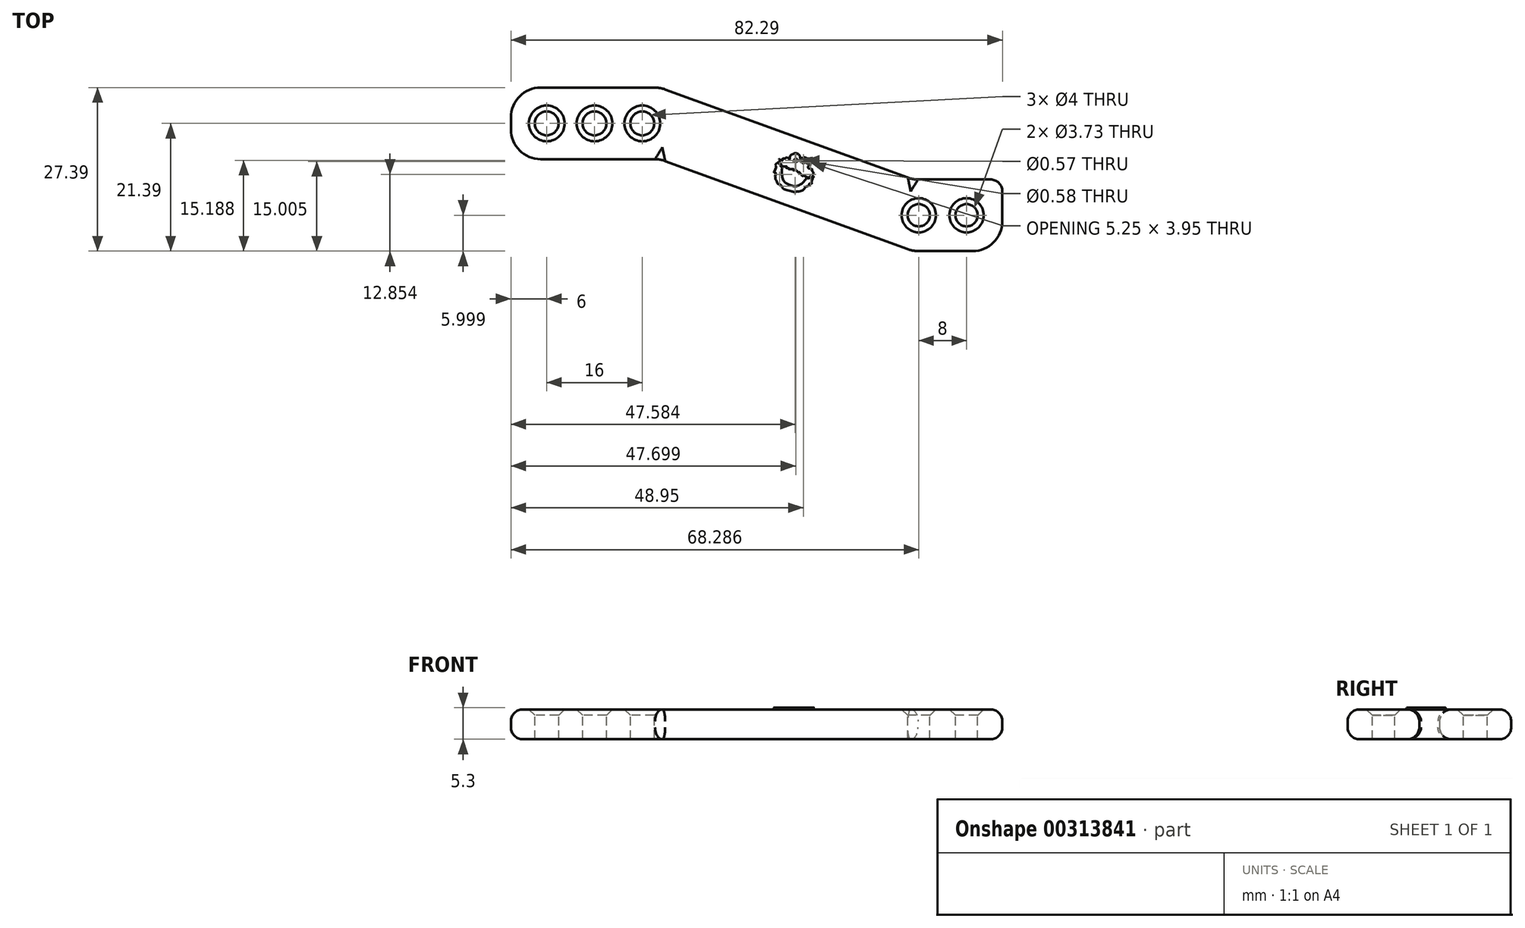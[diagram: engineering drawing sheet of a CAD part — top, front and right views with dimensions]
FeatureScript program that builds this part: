
annotation { "Feature Type Name" : "Feature", "Feature Type Description" : "" }
export const myFeature = defineFeature(function(context is Context, id is Id, definition is map)
    precondition{}
    {
        {
            var Q0;
            Q0=qCreatedBy(makeId("Top.planeOp"),FACE);
            var sketch = newSketch(context, id + "F0", { "sketchPlane" : qUnion([Q0])});
            skLineSegment(sketch, "E0.bottom", {"start": v(0, 0) * mm, "end": v(25, 0) * mm});
            skLineSegment(sketch, "E0.top", {"start": v(0, 12) * mm, "end": v(25, 12) * mm});
            skLineSegment(sketch, "E0.left", {"start": v(0, 0) * mm, "end": v(0, 12) * mm});
            skLineSegment(sketch, "E0.right", {"start": v(25, 0) * mm, "end": v(25, 12) * mm});
            skLineSegment(sketch, "E1.bottom", {"start": v(67.29, -3.4) * mm, "end": v(82.29, -3.4) * mm});
            skLineSegment(sketch, "E1.top", {"start": v(67.29, -15.4) * mm, "end": v(82.29, -15.4) * mm});
            skLineSegment(sketch, "E1.left", {"start": v(67.29, -3.4) * mm, "end": v(67.29, -15.4) * mm});
            skLineSegment(sketch, "E1.right", {"start": v(82.29, -3.4) * mm, "end": v(82.29, -15.4) * mm});
            skLineSegment(sketch, "E2", {"start": v(25, 12) * mm, "end": v(67.29, -3.4) * mm});
            skLineSegment(sketch, "E3", {"start": v(25, 0) * mm, "end": v(67.29, -15.4) * mm});
            skSolve(sketch);
        }
        {
            var Q0;
            Q0=makeQuery(id+"F0.imprint","IMPRINT",FACE,{"disambiguationData":[TD([[makeQuery(id+"F0.imprint","IMPRINT",EDGE,{"derivedFrom":sQuery(id+"F0.wireOp",EDGE,"E0.right")}),-1.0]])]});
            var Q1;
            Q1=makeQuery(id+"F0.imprint","IMPRINT",FACE,{"disambiguationData":[TD([[makeQuery(id+"F0.imprint","IMPRINT",EDGE,{"derivedFrom":sQuery(id+"F0.wireOp",EDGE,"E0.bottom")}),1.0]])]});
            var Q2;
            Q2=makeQuery(id+"F0.imprint","IMPRINT",FACE,{"disambiguationData":[TD([[makeQuery(id+"F0.imprint","IMPRINT",EDGE,{"derivedFrom":sQuery(id+"F0.wireOp",EDGE,"E1.bottom")}),-1.0]])]});
            extrude(context, id + "F1", {"entities" : qUnion([Q0, Q1, Q2]), "depth" : 5 * mm});
        }
        {
            var Q0;
            Q0=makeQuery(id+"F1.opExtrude","CAP_FACE",FACE,{"disambiguationData":[OSD([sQuery(id+"F0.wireOp",EDGE,"E0.bottom"),sQuery(id+"F0.wireOp",EDGE,"E0.top"),sQuery(id+"F0.wireOp",EDGE,"E0.left"),sQuery(id+"F0.wireOp",EDGE,"E1.bottom"),sQuery(id+"F0.wireOp",EDGE,"E1.top"),sQuery(id+"F0.wireOp",EDGE,"E1.right"),sQuery(id+"F0.wireOp",EDGE,"E2"),sQuery(id+"F0.wireOp",EDGE,"E3")])],"isStart":false});
            var sketch = newSketch(context, id + "F2", { "sketchPlane" : qUnion([Q0])});
            skCircle(sketch, "E4", {"center": v(6, 6) * mm, "radius": 2 * mm});
            skCircle(sketch, "E5", {"center": v(76.29, -9.4) * mm, "radius": 1.86 * mm});
            skCircle(sketch, "E6.1.0.0", {"center": v(14, 6) * mm, "radius": 2 * mm});
            skCircle(sketch, "E6.2.0.0", {"center": v(22, 6) * mm, "radius": 2 * mm});
            skLineSegment(sketch, "E6.direction1", {"start": v(6, 6) * mm, "end": v(14, 6) * mm, "construction": true});
            skCircle(sketch, "E7.1.0.0", {"center": v(68.29, -9.4) * mm, "radius": 1.86 * mm});
            skLineSegment(sketch, "E7.direction1", {"start": v(68.29, -9.4) * mm, "end": v(76.29, -9.4) * mm, "construction": true});
            skSolve(sketch);
        }
        {
            var Q0;
            Q0=makeQuery(id+"F2.imprint","IMPRINT",FACE,{"disambiguationData":[TD([[makeQuery(id+"F2.imprint","IMPRINT",EDGE,{"derivedFrom":sQuery(id+"F2.wireOp",EDGE,"E4")}),1.0]])]});
            var Q1;
            Q1=makeQuery(id+"F2.imprint","IMPRINT",FACE,{"disambiguationData":[TD([[makeQuery(id+"F2.imprint","IMPRINT",EDGE,{"derivedFrom":sQuery(id+"F2.wireOp",EDGE,"E6.1.0.0")}),1.0]])]});
            var Q2;
            Q2=makeQuery(id+"F2.imprint","IMPRINT",FACE,{"disambiguationData":[TD([[makeQuery(id+"F2.imprint","IMPRINT",EDGE,{"derivedFrom":sQuery(id+"F2.wireOp",EDGE,"E6.2.0.0")}),1.0]])]});
            var Q3;
            Q3=makeQuery(id+"F2.imprint","IMPRINT",FACE,{"disambiguationData":[TD([[makeQuery(id+"F2.imprint","IMPRINT",EDGE,{"derivedFrom":sQuery(id+"F2.wireOp",EDGE,"E7.1.0.0")}),1.0]])]});
            var Q4;
            Q4=makeQuery(id+"F2.imprint","IMPRINT",FACE,{"disambiguationData":[TD([[makeQuery(id+"F2.imprint","IMPRINT",EDGE,{"derivedFrom":sQuery(id+"F2.wireOp",EDGE,"E5")}),1.0]])]});
            extrude(context, id + "F3", {"entities" : qUnion([Q0, Q1, Q2, Q3, Q4]), "operationType" : NewBodyOperationType.REMOVE, "endBound" : BoundingType.UP_TO_NEXT, "oppositeDirection" : true, "depth" : 3 * mm});
        }
        {
            var Q0;
            Q0=makeQuery(id+"F1.opExtrude","CAP_EDGE",EDGE,{"disambiguationData":[OSD([sQuery(id+"F0.wireOp",EDGE,"E0.bottom")])],"isStart":false});
            var Q1;
            Q1=makeQuery(id+"F1.opExtrude","CAP_EDGE",EDGE,{"disambiguationData":[OSD([sQuery(id+"F0.wireOp",EDGE,"E3")])],"isStart":false});
            var Q2;
            Q2=makeQuery(id+"F1.opExtrude","CAP_EDGE",EDGE,{"disambiguationData":[OSD([sQuery(id+"F0.wireOp",EDGE,"E1.top")])],"isStart":false});
            var Q3;
            Q3=makeQuery(id+"F1.opExtrude","CAP_EDGE",EDGE,{"disambiguationData":[OSD([sQuery(id+"F0.wireOp",EDGE,"E2")])],"isStart":false});
            var Q4;
            Q4=makeQuery(id+"F1.opExtrude","CAP_EDGE",EDGE,{"disambiguationData":[OSD([sQuery(id+"F0.wireOp",EDGE,"E0.top")])],"isStart":false});
            var Q5;
            Q5=makeQuery(id+"F1.opExtrude","CAP_EDGE",EDGE,{"disambiguationData":[OSD([sQuery(id+"F0.wireOp",EDGE,"E1.bottom")])],"isStart":false});
            var Q6;
            Q6=makeQuery(id+"F1.opExtrude","CAP_EDGE",EDGE,{"disambiguationData":[OSD([sQuery(id+"F0.wireOp",EDGE,"E1.bottom")])],"isStart":true});
            var Q7;
            Q7=makeQuery(id+"F1.opExtrude","CAP_EDGE",EDGE,{"disambiguationData":[OSD([sQuery(id+"F0.wireOp",EDGE,"E2")])],"isStart":true});
            var Q8;
            Q8=makeQuery(id+"F1.opExtrude","CAP_EDGE",EDGE,{"disambiguationData":[OSD([sQuery(id+"F0.wireOp",EDGE,"E0.top")])],"isStart":true});
            var Q9;
            Q9=makeQuery(id+"F1.opExtrude","CAP_EDGE",EDGE,{"disambiguationData":[OSD([sQuery(id+"F0.wireOp",EDGE,"E0.bottom")])],"isStart":true});
            var Q10;
            Q10=makeQuery(id+"F1.opExtrude","CAP_EDGE",EDGE,{"disambiguationData":[OSD([sQuery(id+"F0.wireOp",EDGE,"E3")])],"isStart":true});
            var Q11;
            Q11=makeQuery(id+"F1.opExtrude","CAP_EDGE",EDGE,{"disambiguationData":[OSD([sQuery(id+"F0.wireOp",EDGE,"E1.top")])],"isStart":true});
            var Q12;
            Q12=makeQuery(id+"F1.opExtrude","SWEPT_EDGE",EDGE,{"disambiguationData":[OSD([sQuery(id+"F0.wireOp",EDGE,"E1.bottom"),sQuery(id+"F0.wireOp",EDGE,"E1.right")])]});
            var Q13;
            Q13=makeQuery(id+"F1.opExtrude","CAP_EDGE",EDGE,{"disambiguationData":[OSD([sQuery(id+"F0.wireOp",EDGE,"E0.left")])],"isStart":true});
            var Q14;
            Q14=makeQuery(id+"F1.opExtrude","CAP_EDGE",EDGE,{"disambiguationData":[OSD([sQuery(id+"F0.wireOp",EDGE,"E0.left")])],"isStart":false});
            var Q15;
            Q15=makeQuery(id+"F1.opExtrude","CAP_EDGE",EDGE,{"disambiguationData":[OSD([sQuery(id+"F0.wireOp",EDGE,"E1.right")])],"isStart":false});
            var Q16;
            Q16=makeQuery(id+"F1.opExtrude","CAP_EDGE",EDGE,{"disambiguationData":[OSD([sQuery(id+"F0.wireOp",EDGE,"E1.right")])],"isStart":true});
            fillet(context, id + "F4", {"entities" : qUnion([Q0, Q1, Q2, Q3, Q4, Q5, Q6, Q7, Q8, Q9, Q10, Q11, Q12, Q13, Q14, Q15, Q16]), "radius" : 2 * mm, "tangentPropagation" : true, "allowEdgeOverflow" : false});
        }
        {
            var Q0;
            Q0=makeQuery(id+"F1.opExtrude","SWEPT_EDGE",EDGE,{"disambiguationData":[OSD([sQuery(id+"F0.wireOp",EDGE,"E1.top"),sQuery(id+"F0.wireOp",EDGE,"E1.left"),sQuery(id+"F0.wireOp",EDGE,"E3")])]});
            var Q1;
            Q1=makeQuery(id+"F1.opExtrude","SWEPT_EDGE",EDGE,{"disambiguationData":[OSD([sQuery(id+"F0.wireOp",EDGE,"E1.top"),sQuery(id+"F0.wireOp",EDGE,"E1.right")])]});
            var Q2;
            Q2=makeQuery(id+"F1.opExtrude","SWEPT_EDGE",EDGE,{"disambiguationData":[OSD([sQuery(id+"F0.wireOp",EDGE,"E0.bottom"),sQuery(id+"F0.wireOp",EDGE,"E0.right"),sQuery(id+"F0.wireOp",EDGE,"E3")])]});
            var Q3;
            Q3=makeQuery(id+"F1.opExtrude","SWEPT_EDGE",EDGE,{"disambiguationData":[OSD([sQuery(id+"F0.wireOp",EDGE,"E0.bottom"),sQuery(id+"F0.wireOp",EDGE,"E0.left")])]});
            var Q4;
            Q4=makeQuery(id+"F1.opExtrude","SWEPT_EDGE",EDGE,{"disambiguationData":[OSD([sQuery(id+"F0.wireOp",EDGE,"E0.top"),sQuery(id+"F0.wireOp",EDGE,"E0.left")])]});
            var Q5;
            Q5=makeQuery(id+"F1.opExtrude","SWEPT_EDGE",EDGE,{"disambiguationData":[OSD([sQuery(id+"F0.wireOp",EDGE,"E0.top"),sQuery(id+"F0.wireOp",EDGE,"E0.right"),sQuery(id+"F0.wireOp",EDGE,"E2")])]});
            var Q6;
            Q6=makeQuery(id+"F1.opExtrude","SWEPT_EDGE",EDGE,{"disambiguationData":[OSD([sQuery(id+"F0.wireOp",EDGE,"E1.bottom"),sQuery(id+"F0.wireOp",EDGE,"E1.left"),sQuery(id+"F0.wireOp",EDGE,"E2")])]});
            var Q7;
            {var subQ0=sQuery(id+"F0.wireOp",EDGE,"E1.right");Q7=makeQuery(id+"F4.opFillet","BLEND_EDGE",EDGE,{"blendedFrom":[makeQuery(id+"F1.opExtrude","SWEPT_EDGE",EDGE,{"disambiguationData":[OSD([sQuery(id+"F0.wireOp",EDGE,"E1.bottom"),subQ0])]}),makeQuery(id+"F1.opExtrude","SWEPT_FACE",FACE,{"disambiguationData":[OSD([subQ0])]})],"blendedInto":[makeQuery(id+"F1.opExtrude","SWEPT_FACE",FACE,{"disambiguationData":[OSD([subQ0])]})]});}
            var Q8;
            {var subQ0=sQuery(id+"F0.wireOp",EDGE,"E1.bottom");Q8=makeQuery(id+"F4.opFillet","BLEND_EDGE",EDGE,{"blendedFrom":[makeQuery(id+"F1.opExtrude","SWEPT_EDGE",EDGE,{"disambiguationData":[OSD([subQ0,sQuery(id+"F0.wireOp",EDGE,"E1.right")])]}),makeQuery(id+"F1.opExtrude","SWEPT_FACE",FACE,{"disambiguationData":[OSD([subQ0])]})],"blendedInto":[makeQuery(id+"F1.opExtrude","SWEPT_FACE",FACE,{"disambiguationData":[OSD([subQ0])]})]});}
            fillet(context, id + "F5", {"entities" : qUnion([Q0, Q1, Q2, Q3, Q4, Q5, Q6, Q7, Q8]), "radius" : 5 * mm, "tangentPropagation" : true, "allowEdgeOverflow" : false});
        }
        {
            var Q0;
            Q0=makeQuery(id+"F3.boolean.opBoolean","COPY",EDGE,{"derivedFrom":makeQuery(id+"F3.opExtrude","CAP_EDGE",EDGE,{"disambiguationData":[OSD([sQuery(id+"F2.wireOp",EDGE,"E4")])],"isStart":true})});
            var Q1;
            Q1=makeQuery(id+"F3.boolean.opBoolean","COPY",EDGE,{"derivedFrom":makeQuery(id+"F3.opExtrude","CAP_EDGE",EDGE,{"disambiguationData":[OSD([sQuery(id+"F2.wireOp",EDGE,"E6.1.0.0")])],"isStart":true})});
            var Q2;
            Q2=makeQuery(id+"F3.boolean.opBoolean","COPY",EDGE,{"derivedFrom":makeQuery(id+"F3.opExtrude","CAP_EDGE",EDGE,{"disambiguationData":[OSD([sQuery(id+"F2.wireOp",EDGE,"E6.2.0.0")])],"isStart":true})});
            var Q3;
            Q3=makeQuery(id+"F3.boolean.opBoolean","COPY",EDGE,{"derivedFrom":makeQuery(id+"F3.opExtrude","CAP_EDGE",EDGE,{"disambiguationData":[OSD([sQuery(id+"F2.wireOp",EDGE,"E7.1.0.0")])],"isStart":true})});
            var Q4;
            Q4=makeQuery(id+"F3.boolean.opBoolean","COPY",EDGE,{"derivedFrom":makeQuery(id+"F3.opExtrude","CAP_EDGE",EDGE,{"disambiguationData":[OSD([sQuery(id+"F2.wireOp",EDGE,"E5")])],"isStart":true})});
            var Q5;
            Q5=makeQuery(id+"F1.opExtrude","CAP_FACE",FACE,{"disambiguationData":[OSD([sQuery(id+"F0.wireOp",EDGE,"E0.bottom"),sQuery(id+"F0.wireOp",EDGE,"E0.top"),sQuery(id+"F0.wireOp",EDGE,"E0.left"),sQuery(id+"F0.wireOp",EDGE,"E1.bottom"),sQuery(id+"F0.wireOp",EDGE,"E1.top"),sQuery(id+"F0.wireOp",EDGE,"E1.right"),sQuery(id+"F0.wireOp",EDGE,"E2"),sQuery(id+"F0.wireOp",EDGE,"E3")])],"isStart":false});
            chamfer(context, id + "F6", {"entities" : qUnion([Q0, Q1, Q2, Q3, Q4, Q5]), "width" : 1 * mm, "tangentPropagation" : true});
        }
        {
            var Q0;
            Q0=makeQuery(id+"F1.opExtrude","CAP_FACE",FACE,{"disambiguationData":[OSD([sQuery(id+"F0.wireOp",EDGE,"E0.bottom"),sQuery(id+"F0.wireOp",EDGE,"E0.top"),sQuery(id+"F0.wireOp",EDGE,"E0.left"),sQuery(id+"F0.wireOp",EDGE,"E1.bottom"),sQuery(id+"F0.wireOp",EDGE,"E1.top"),sQuery(id+"F0.wireOp",EDGE,"E1.right"),sQuery(id+"F0.wireOp",EDGE,"E2"),sQuery(id+"F0.wireOp",EDGE,"E3")])],"isStart":false});
            var sketch = newSketch(context, id + "F7", { "sketchPlane" : qUnion([Q0])});
            skFitSpline(sketch, "E8", {"points": [v(47.54, 1) * mm, v(47.95, 0.94) * mm, v(48.28, 0.67) * mm, v(48.38, 0.5) * mm, v(48.44, 0.23) * mm, v(48.5, 0) * mm, v(48.85, 0.26) * mm, v(49.3, 0.26) * mm], "startDerivative": vector(2.67, 0.04) * mm, "endDerivative": vector(2.8, -0.72) * mm});
            skFitSpline(sketch, "E9", {"points": [v(49.3, 0.26) * mm, v(49.62, 0.13) * mm, v(49.9, -0.14) * mm, v(50.05, -0.45) * mm, v(50.05, -0.81) * mm, v(49.94, -1.06) * mm], "startDerivative": vector(1.62, -0.46) * mm, "endDerivative": vector(-0.7, -1.27) * mm});
            skFitSpline(sketch, "E10", {"points": [v(49.74, -1.22) * mm, v(49.94, -1.06) * mm], "startDerivative": vector(0.2, 0.17) * mm, "endDerivative": vector(0.2, 0.17) * mm});
            skPoint(sketch, "E11.12.internal.snap0", {"position": v(50.73, -3.51) * mm});
            skFitSpline(sketch, "E11", {"points": [v(49.74, -1.22) * mm, v(49.74, -1.42) * mm, v(50.05, -1.6) * mm, v(50.35, -1.67) * mm, v(50.48, -1.76) * mm, v(50.37, -1.9) * mm, v(50.61, -2.13) * mm, v(50.61, -2.5) * mm, v(50.54, -2.83) * mm, v(50.72, -2.98) * mm, v(50.5, -3.04) * mm, v(50.5, -3.13) * mm, v(50.45, -3.51) * mm, v(50.3, -3.71) * mm, v(50.39, -4.08) * mm, v(50.05, -4.08) * mm, v(49.94, -4.14) * mm, v(49.94, -4.32) * mm, v(49.74, -4.54) * mm], "startDerivative": vector(-1.07, -4.28) * mm, "endDerivative": vector(-4.48, -3.36) * mm});
            skFitSpline(sketch, "E12", {"points": [v(49.74, -4.54) * mm, v(49.5, -4.54) * mm, v(49.3, -4.7) * mm, v(49.07, -5) * mm, v(48.8, -5.26) * mm, v(48.22, -5.4) * mm, v(47.87, -5.4) * mm, v(47.8, -5.4) * mm, v(47.64, -5.55) * mm, v(47.2, -5.4) * mm, v(47.06, -5.4) * mm, v(46.48, -5.24) * mm, v(45.96, -5.07) * mm], "startDerivative": vector(-3.63, 0.54) * mm, "endDerivative": vector(-4.47, 1.45) * mm});
            skFitSpline(sketch, "E13", {"points": [v(45.96, -5.07) * mm, v(45.6, -4.9) * mm, v(45.35, -4.54) * mm, v(44.98, -4.2) * mm, v(44.7, -4.1) * mm, v(44.52, -3.73) * mm, v(44.26, -3.3) * mm, v(44.32, -3.07) * mm, v(44.25, -2.92) * mm, v(44.3, -2.26) * mm, v(44, -2.16) * mm, v(44.13, -1.97) * mm, v(44.37, -1.22) * mm, v(44.2, -1.01) * mm, v(44.18, -1.06) * mm], "startDerivative": vector(-5.3, 1.59) * mm, "endDerivative": vector(-0.14, -2.38) * mm});
            skFitSpline(sketch, "E14", {"points": [v(44.2, -1.01) * mm, v(44.75, -0.5) * mm, v(45.07, -0.3) * mm, v(44.89, 0) * mm, v(45.4, -0.2) * mm, v(45.53, -0.14) * mm, v(45.4, 0) * mm, v(45.71, 0.13) * mm, v(45.96, 0.13) * mm, v(46.11, 0.26) * mm, v(46.32, 0.26) * mm, v(46.7, 0) * mm, v(46.72, 0.26) * mm, v(46.87, 0.65) * mm, v(47.54, 1) * mm, v(47.68, 1) * mm], "startDerivative": vector(5.05, 6.18) * mm, "endDerivative": vector(2.46, -0.43) * mm});
            skCircle(sketch, "E15", {"center": v(47.7, -0.2) * mm, "radius": 0.29 * mm});
            skCircle(sketch, "E16", {"center": v(48.95, -0.39) * mm, "radius": 0.29 * mm});
            skFitSpline(sketch, "E17", {"points": [v(45.04, -0.56) * mm, v(45.19, -0.63) * mm, v(45.19, -0.8) * mm, v(45.57, -1.23) * mm], "startDerivative": vector(0.77, -0.18) * mm, "endDerivative": vector(1.12, -0.94) * mm});
            skFitSpline(sketch, "E18", {"points": [v(45.57, -1.23) * mm, v(46.17, -1.23) * mm, v(46.06, -1.4) * mm, v(46.56, -1.53) * mm, v(46.5, -1.66) * mm, v(47.38, -1.7) * mm, v(47.21, -1.82) * mm, v(47.77, -1.86) * mm, v(47.87, -1.93) * mm, v(48.2, -2.31) * mm], "startDerivative": vector(6.63, 0.77) * mm, "endDerivative": vector(3.2, -3.53) * mm});
            skFitSpline(sketch, "E19", {"points": [v(48.2, -2.31) * mm, v(48.32, -2.15) * mm, v(48.39, -2.31) * mm, v(48.94, -2.85) * mm, v(48.92, -2.63) * mm, v(49.13, -2.8) * mm, v(50, -3.01) * mm, v(50.07, -2.85) * mm, v(50.2, -2.9) * mm, v(50.17, -3.17) * mm, v(50.07, -3.12) * mm, v(49.95, -3.19) * mm, v(49.51, -3.15) * mm], "startDerivative": vector(2.14, 3.4) * mm, "endDerivative": vector(-4.9, 1.22) * mm});
            skFitSpline(sketch, "E20", {"points": [v(49.51, -3.15) * mm, v(48.98, -3.83) * mm, v(48.2, -4.38) * mm, v(47.5, -4.51) * mm, v(46.61, -4.3) * mm, v(46.04, -4) * mm], "startDerivative": vector(-2.31, -3.42) * mm, "endDerivative": vector(-2.94, 1.75) * mm});
            skFitSpline(sketch, "E21", {"points": [v(46.04, -4) * mm, v(45.57, -3.45) * mm, v(45.4, -2.76) * mm, v(45.35, -2.05) * mm, v(45.35, -1.23) * mm, v(45.19, -1.23) * mm, v(45.04, -0.8) * mm, v(44.91, -0.8) * mm, v(45.04, -0.56) * mm], "startDerivative": vector(-3.44, 3.2) * mm, "endDerivative": vector(2.32, 3.56) * mm});
            skSolve(sketch);
        }
        {
            var Q0;
            {var subQ1=sQuery(id+"F7.wireOp",EDGE,"E8");Q0=makeQuery(id+"F7.imprint","IMPRINT",FACE,{"disambiguationData":[TD([[makeQuery(id+"F7.imprint","IMPRINT",EDGE,{"derivedFrom":subQ1}),-1.0]])]});}
            extrude(context, id + "F8", {"entities" : qUnion([Q0]), "depth" : .3 * mm});
        }
    });
